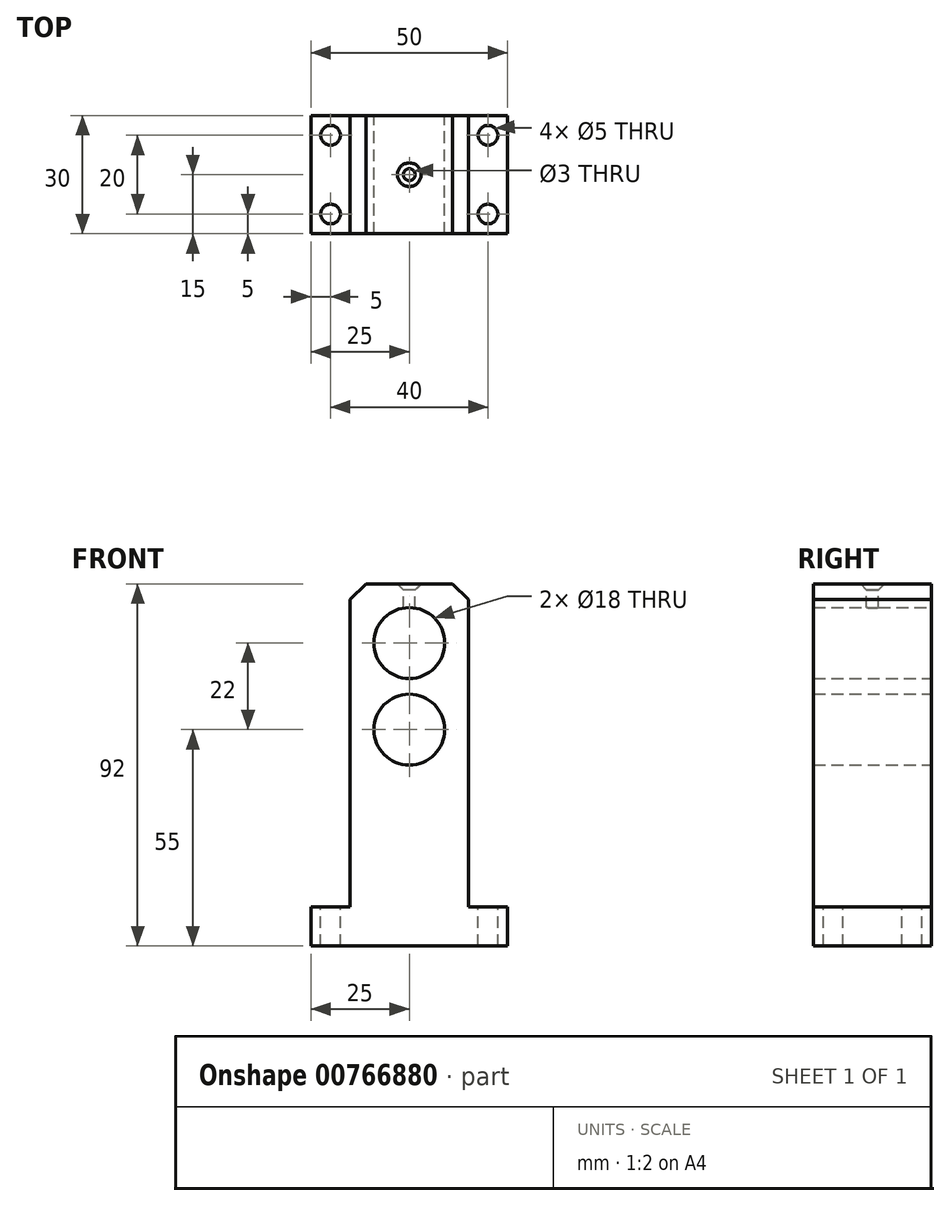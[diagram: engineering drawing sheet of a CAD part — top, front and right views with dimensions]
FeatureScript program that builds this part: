
annotation { "Feature Type Name" : "Feature", "Feature Type Description" : "" }
export const myFeature = defineFeature(function(context is Context, id is Id, definition is map)
    precondition{}
    {
        {
            var Q0;
            Q0=qCreatedBy(makeId("Front.planeOp"),FACE);
            var sketch = newSketch(context, id + "F0", { "sketchPlane" : qUnion([Q0])});
            skLineSegment(sketch, "E0", {"start": v(0, 0) * mm, "end": v(50, 0) * mm});
            skLineSegment(sketch, "E1", {"start": v(50, 0) * mm, "end": v(50, 10) * mm});
            skLineSegment(sketch, "E2", {"start": v(50, 10) * mm, "end": v(40, 10) * mm});
            skLineSegment(sketch, "E3", {"start": v(40, 10) * mm, "end": v(40, 92) * mm});
            skLineSegment(sketch, "E4", {"start": v(40, 92) * mm, "end": v(10, 92) * mm});
            skLineSegment(sketch, "E5", {"start": v(10, 92) * mm, "end": v(10, 10) * mm});
            skLineSegment(sketch, "E6", {"start": v(10, 10) * mm, "end": v(0, 10) * mm});
            skLineSegment(sketch, "E7", {"start": v(0, 10) * mm, "end": v(0, 0) * mm});
            skCircle(sketch, "E8", {"center": v(25, 77) * mm, "radius": 9 * mm});
            skCircle(sketch, "E9", {"center": v(25, 55) * mm, "radius": 9 * mm});
            skSolve(sketch);
        }
        {
            var Q0;
            Q0=makeQuery(id+"F0.imprint","IMPRINT",FACE,{"disambiguationData":[TD([[makeQuery(id+"F0.imprint","IMPRINT",EDGE,{"derivedFrom":sQuery(id+"F0.wireOp",EDGE,"E0")}),1.0]])]});
            extrude(context, id + "F1", {"entities" : qUnion([Q0]), "depth" : 15 * mm, "offsetDistance" : 25 * mm, "hasSecondDirection" : true, "secondDirectionOppositeDirection" : true, "secondDirectionDepth" : 15 * mm});
        }
        {
            var Q0;
            Q0=makeQuery(id+"F1.opExtrude","SWEPT_EDGE",EDGE,{"disambiguationData":[OSD([sQuery(id+"F0.wireOp",EDGE,"E3"),sQuery(id+"F0.wireOp",EDGE,"E4")])]});
            var Q1;
            Q1=makeQuery(id+"F1.opExtrude","SWEPT_EDGE",EDGE,{"disambiguationData":[OSD([sQuery(id+"F0.wireOp",EDGE,"E4"),sQuery(id+"F0.wireOp",EDGE,"E5")])]});
            chamfer(context, id + "F2", {"entities" : qUnion([Q0, Q1]), "width" : 4 * mm, "tangentPropagation" : true});
        }
        {
            var Q0;
            Q0=makeQuery(id+"F1.opExtrude","SWEPT_FACE",FACE,{"disambiguationData":[OSD([sQuery(id+"F0.wireOp",EDGE,"E4")])]});
            var sketch = newSketch(context, id + "F3", { "sketchPlane" : qUnion([Q0])});
            skPoint(sketch, "E10", {"position": v(25, 0) * mm});
            skSolve(sketch);
        }
        {
            var Q0;
            Q0=sQuery(id+"F3.wireOp",VERTEX,"E10");
            var Q1;
            Q1=makeQuery(id+"F1.opExtrude","SWEPT_BODY",BODY,{"disambiguationData":[OSD([sQuery(id+"F0.wireOp",EDGE,"E0"),sQuery(id+"F0.wireOp",EDGE,"E1"),sQuery(id+"F0.wireOp",EDGE,"E2"),sQuery(id+"F0.wireOp",EDGE,"E3"),sQuery(id+"F0.wireOp",EDGE,"E4"),sQuery(id+"F0.wireOp",EDGE,"E5"),sQuery(id+"F0.wireOp",EDGE,"E6"),sQuery(id+"F0.wireOp",EDGE,"E7"),sQuery(id+"F0.wireOp",EDGE,"E8"),sQuery(id+"F0.wireOp",EDGE,"E9")])]});
            hole(context, id + "F4", {"style" : HoleStyle.C_SINK, "endStyle" : HoleEndStyle.BLIND, "holeDiameter" : 3 * mm, "cSinkDiameter" : 6 * mm, "cSinkAngle" : 90 * degree, "majorDiameter" : 5 * mm, "holeDepth" : 10 * mm, "isTappedThrough" : true, "tappedDepth" : 12 * mm, "tapClearance" : 3, "locations" : qUnion([Q0]), "scope" : qUnion([Q1])});
        }
        {
            var Q0;
            Q0=makeQuery(id+"F1.opExtrude","SWEPT_FACE",FACE,{"disambiguationData":[OSD([sQuery(id+"F0.wireOp",EDGE,"E6")])]});
            var sketch = newSketch(context, id + "F5", { "sketchPlane" : qUnion([Q0])});
            skCircle(sketch, "E11", {"center": v(5, 10) * mm, "radius": 2.5 * mm});
            skCircle(sketch, "E12", {"center": v(45, 10) * mm, "radius": 2.5 * mm});
            skCircle(sketch, "E13", {"center": v(45, -10) * mm, "radius": 2.5 * mm});
            skCircle(sketch, "E14", {"center": v(5, -10) * mm, "radius": 2.5 * mm});
            skSolve(sketch);
        }
        {
            var Q0;
            Q0=makeQuery(id+"F5.imprint","IMPRINT",FACE,{"disambiguationData":[TD([[makeQuery(id+"F5.imprint","IMPRINT",EDGE,{"derivedFrom":sQuery(id+"F5.wireOp",EDGE,"E11")}),1.0]])]});
            var Q1;
            Q1=makeQuery(id+"F5.imprint","IMPRINT",FACE,{"disambiguationData":[TD([[makeQuery(id+"F5.imprint","IMPRINT",EDGE,{"derivedFrom":sQuery(id+"F5.wireOp",EDGE,"E14")}),1.0]])]});
            var Q2;
            Q2=makeQuery(id+"F5.imprint","IMPRINT",FACE,{"disambiguationData":[TD([[makeQuery(id+"F5.imprint","IMPRINT",EDGE,{"derivedFrom":sQuery(id+"F5.wireOp",EDGE,"E13")}),1.0]])]});
            var Q3;
            Q3=makeQuery(id+"F5.imprint","IMPRINT",FACE,{"disambiguationData":[TD([[makeQuery(id+"F5.imprint","IMPRINT",EDGE,{"derivedFrom":sQuery(id+"F5.wireOp",EDGE,"E12")}),1.0]])]});
            extrude(context, id + "F6", {"entities" : qUnion([Q0, Q1, Q2, Q3]), "operationType" : NewBodyOperationType.REMOVE, "oppositeDirection" : true, "depth" : 10 * mm, "offsetDistance" : 25 * mm});
        }
    });
